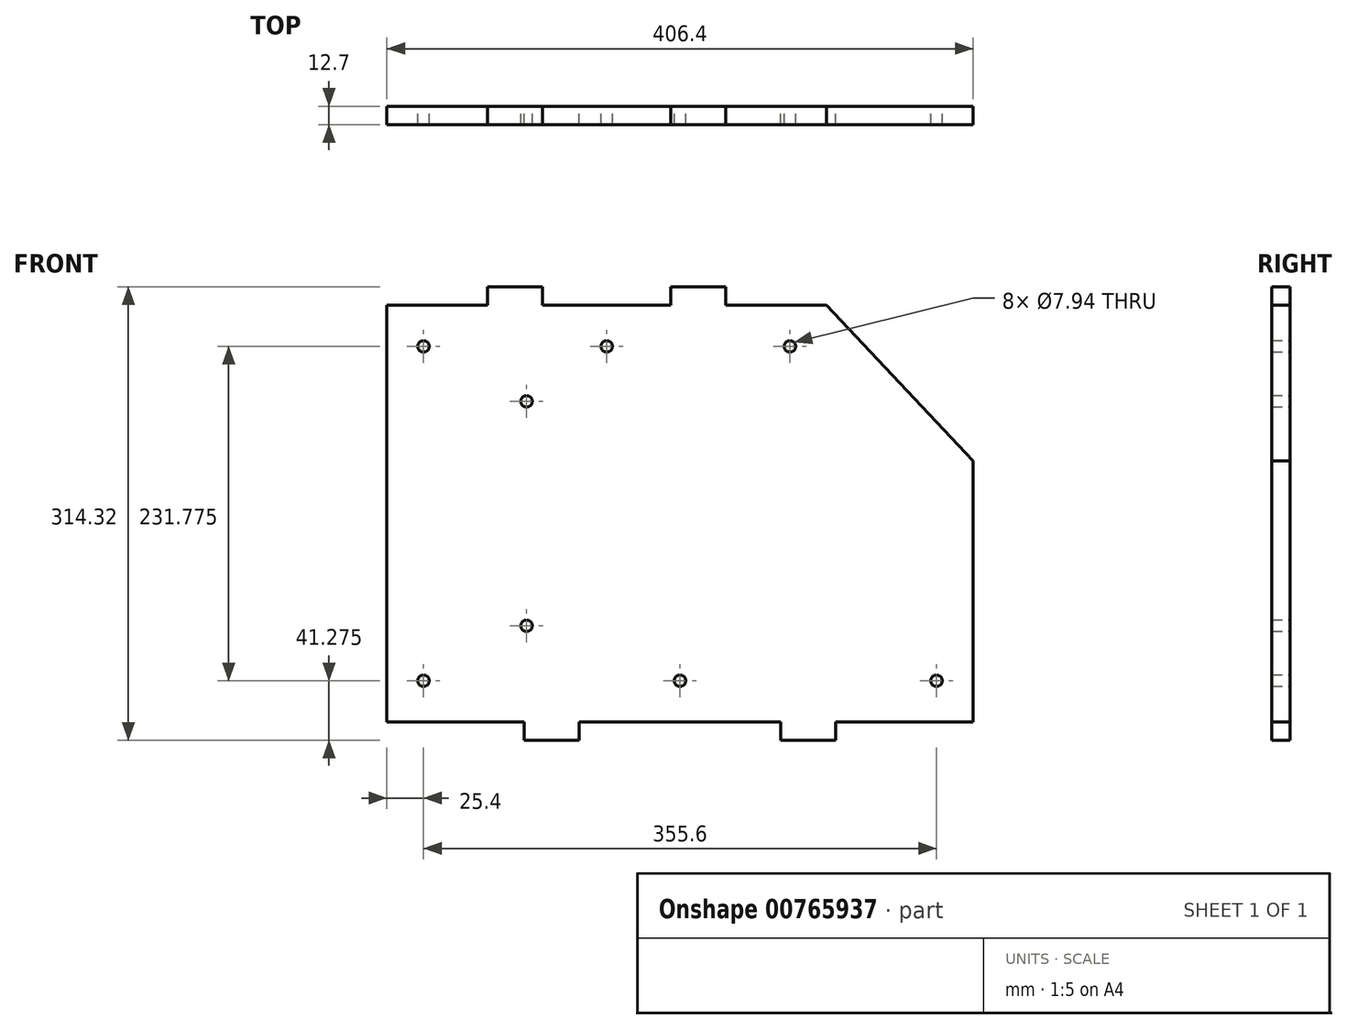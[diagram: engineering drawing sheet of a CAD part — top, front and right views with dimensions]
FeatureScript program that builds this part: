
annotation { "Feature Type Name" : "Feature", "Feature Type Description" : "" }
export const myFeature = defineFeature(function(context is Context, id is Id, definition is map)
    precondition{}
    {
        {
            var Q0;
            Q0=qCreatedBy(makeId("Front.planeOp"),FACE);
            var sketch = newSketch(context, id + "F0", { "sketchPlane" : qUnion([Q0])});
            skLineSegment(sketch, "E0", {"start": v(0, 0) * mm, "end": v(0, 288.93) * mm});
            skLineSegment(sketch, "E1", {"start": v(0, 288.93) * mm, "end": v(304.8, 288.93) * mm});
            skLineSegment(sketch, "E2", {"start": v(304.8, 288.93) * mm, "end": v(406.4, 180.97) * mm});
            skLineSegment(sketch, "E3", {"start": v(406.4, 180.98) * mm, "end": v(406.4, 0) * mm});
            skLineSegment(sketch, "E4", {"start": v(406.4, 0) * mm, "end": v(0, 0) * mm});
            skLineSegment(sketch, "E5", {"start": v(0, 260.35) * mm, "end": v(331.7, 260.35) * mm, "construction": true});
            skLineSegment(sketch, "E6", {"start": v(0, 28.57) * mm, "end": v(406.4, 28.58) * mm, "construction": true});
            skPoint(sketch, "E7", {"position": v(25.4, 260.35) * mm});
            skPoint(sketch, "E8", {"position": v(279.4, 260.35) * mm});
            skPoint(sketch, "E9", {"position": v(152.4, 260.35) * mm});
            skPoint(sketch, "E10", {"position": v(25.4, 28.57) * mm});
            skPoint(sketch, "E11", {"position": v(381, 28.58) * mm});
            skPoint(sketch, "E12", {"position": v(203.2, 28.57) * mm});
            skLineSegment(sketch, "E13", {"start": v(152.4, 288.93) * mm, "end": v(152.4, 0) * mm, "construction": true});
            skLineSegment(sketch, "E14", {"start": v(203.2, 0) * mm, "end": v(203.2, 288.93) * mm, "construction": true});
            skLineSegment(sketch, "E15", {"start": v(88.9, 288.93) * mm, "end": v(88.9, 238.42) * mm, "construction": true});
            skLineSegment(sketch, "E16", {"start": v(114.3, 0) * mm, "end": v(114.3, 73.95) * mm, "construction": true});
            skLineSegment(sketch, "E17.bottom", {"start": v(107.95, 276.23) * mm, "end": v(69.85, 276.23) * mm});
            skLineSegment(sketch, "E17.top", {"start": v(107.95, 301.63) * mm, "end": v(69.85, 301.63) * mm});
            skLineSegment(sketch, "E17.left", {"start": v(107.95, 276.23) * mm, "end": v(107.95, 301.63) * mm});
            skLineSegment(sketch, "E17.right", {"start": v(69.85, 276.23) * mm, "end": v(69.85, 301.63) * mm});
            skPoint(sketch, "E17.middle", {"position": v(88.9, 288.93) * mm});
            skLineSegment(sketch, "E18.bottom", {"start": v(133.35, -12.7) * mm, "end": v(95.25, -12.7) * mm});
            skLineSegment(sketch, "E18.top", {"start": v(133.35, 12.7) * mm, "end": v(95.25, 12.7) * mm});
            skLineSegment(sketch, "E18.left", {"start": v(133.35, -12.7) * mm, "end": v(133.35, 12.7) * mm});
            skLineSegment(sketch, "E18.right", {"start": v(95.25, -12.7) * mm, "end": v(95.25, 12.7) * mm});
            skPoint(sketch, "E18.middle", {"position": v(114.3, 0) * mm});
            skLineSegment(sketch, "E19.MirrorCS", {"start": v(304.8, 288.93) * mm, "end": v(0, 288.93) * mm});
            skLineSegment(sketch, "E20.MirrorCS", {"start": v(196.85, 276.23) * mm, "end": v(196.85, 301.63) * mm});
            skLineSegment(sketch, "E21.MirrorCS", {"start": v(196.85, 301.63) * mm, "end": v(234.95, 301.63) * mm});
            skLineSegment(sketch, "E22.MirrorCS", {"start": v(234.95, 276.23) * mm, "end": v(234.95, 301.63) * mm});
            skLineSegment(sketch, "E23.MirrorCS", {"start": v(196.85, 276.23) * mm, "end": v(234.95, 276.23) * mm});
            skLineSegment(sketch, "E24.MirrorCS", {"start": v(273.05, 12.7) * mm, "end": v(311.15, 12.7) * mm});
            skLineSegment(sketch, "E25.MirrorCS", {"start": v(311.15, -12.7) * mm, "end": v(311.15, 12.7) * mm});
            skLineSegment(sketch, "E26.MirrorCS", {"start": v(273.05, -12.7) * mm, "end": v(273.05, 12.7) * mm});
            skLineSegment(sketch, "E27.MirrorCS", {"start": v(273.05, -12.7) * mm, "end": v(311.15, -12.7) * mm});
            skLineSegment(sketch, "E28", {"start": v(96.84, 0) * mm, "end": v(96.84, 288.93) * mm, "construction": true});
            skLineSegment(sketch, "E29", {"start": v(0, 144.46) * mm, "end": v(96.84, 144.46) * mm, "construction": true});
            skPoint(sketch, "E30", {"position": v(96.84, 66.68) * mm});
            skPoint(sketch, "E31.MirrorP", {"position": v(96.84, 222.25) * mm});
            skSolve(sketch);
        }
        {
            var Q0;
            Q0 = qSketchRegion(id + "F0", true);
            var Q1;
            Q1=makeQuery(id+"F0.imprint","IMPRINT",FACE,{"disambiguationData":[TD([[makeQuery(id+"F0.imprint","IMPRINT",EDGE,{"derivedFrom":sQuery(id+"F0.wireOp",EDGE,"E0")}),-1.0]])]});
            extrude(context, id + "F1", {"entities" : qUnion([Q0, Q1]), "depth" : 12.7 * mm, "offsetDistance" : 25.4 * mm});
        }
        {
            var Q0;
            Q0=sQuery(id+"F0.wireOp",VERTEX,"E7");
            var Q1;
            Q1=sQuery(id+"F0.wireOp",VERTEX,"E9");
            var Q2;
            Q2=sQuery(id+"F0.wireOp",VERTEX,"E8");
            var Q3;
            Q3=sQuery(id+"F0.wireOp",VERTEX,"E11");
            var Q4;
            Q4=sQuery(id+"F0.wireOp",VERTEX,"E12");
            var Q5;
            Q5=sQuery(id+"F0.wireOp",VERTEX,"E10");
            var Q6;
            Q6=makeQuery(id+"F1.opExtrude","SWEPT_BODY",BODY,{"disambiguationData":[OSD([sQuery(id+"F0.wireOp",EDGE,"E0"),sQuery(id+"F0.wireOp",EDGE,"E1"),sQuery(id+"F0.wireOp",EDGE,"E2"),sQuery(id+"F0.wireOp",EDGE,"E3"),sQuery(id+"F0.wireOp",EDGE,"E4")])]});
            hole(context, id + "F2", {"style" : HoleStyle.SIMPLE, "endStyle" : HoleEndStyle.BLIND, "oppositeDirection" : true, "standardTappedOrClearance" : lookupTablePath({ "standard" : "ANSI", "engagement" : "75%", "pitch" : "16 tpi", "size" : "3/8", "type" : "Tapped" }), "standardBlindInLast" : lookupTablePath({ "standard" : "ANSI", "engagement" : "75%", "pitch" : "16 tpi", "size" : "3/8", "type" : "Tapped" }), "holeDiameter" : 7.94 * mm, "majorDiameter" : 9.52 * mm, "showTappedDepth" : true, "holeDepth" : 20.66 * mm, "isTappedThrough" : true, "tappedDepth" : 15.9 * mm, "tapClearance" : 3, "locations" : qUnion([Q0, Q1, Q2, Q3, Q4, Q5]), "scope" : qUnion([Q6])});
        }
        {
            var Q0;
            Q0=sQuery(id+"F0.wireOp",VERTEX,"E31.MirrorP");
            var Q1;
            Q1=sQuery(id+"F0.wireOp",VERTEX,"E30");
            var Q2;
            Q2=makeQuery(id+"F1.opExtrude","SWEPT_BODY",BODY,{"disambiguationData":[OSD([sQuery(id+"F0.wireOp",EDGE,"E0"),sQuery(id+"F0.wireOp",EDGE,"E2"),sQuery(id+"F0.wireOp",EDGE,"E3"),sQuery(id+"F0.wireOp",EDGE,"E4"),sQuery(id+"F0.wireOp",EDGE,"E17.top"),sQuery(id+"F0.wireOp",EDGE,"E17.left"),sQuery(id+"F0.wireOp",EDGE,"E17.right"),sQuery(id+"F0.wireOp",EDGE,"E18.bottom"),sQuery(id+"F0.wireOp",EDGE,"E18.left"),sQuery(id+"F0.wireOp",EDGE,"E18.right"),sQuery(id+"F0.wireOp",EDGE,"E19.MirrorCS"),sQuery(id+"F0.wireOp",EDGE,"E20.MirrorCS"),sQuery(id+"F0.wireOp",EDGE,"E21.MirrorCS"),sQuery(id+"F0.wireOp",EDGE,"E22.MirrorCS"),sQuery(id+"F0.wireOp",EDGE,"E25.MirrorCS"),sQuery(id+"F0.wireOp",EDGE,"E26.MirrorCS"),sQuery(id+"F0.wireOp",EDGE,"E27.MirrorCS")])]});
            hole(context, id + "F3", {"style" : HoleStyle.SIMPLE, "endStyle" : HoleEndStyle.BLIND, "oppositeDirection" : true, "standardTappedOrClearance" : lookupTablePath({ "standard" : "ANSI", "engagement" : "75%", "pitch" : "16 tpi", "size" : "3/8", "type" : "Tapped" }), "standardBlindInLast" : lookupTablePath({ "standard" : "ANSI", "engagement" : "75%", "pitch" : "16 tpi", "size" : "3/8", "type" : "Tapped" }), "holeDiameter" : 7.94 * mm, "majorDiameter" : 9.52 * mm, "showTappedDepth" : true, "holeDepth" : 17.51 * mm, "isTappedThrough" : true, "tappedDepth" : 12.75 * mm, "tapClearance" : 3, "locations" : qUnion([Q0, Q1]), "scope" : qUnion([Q2])});
        }
    });
